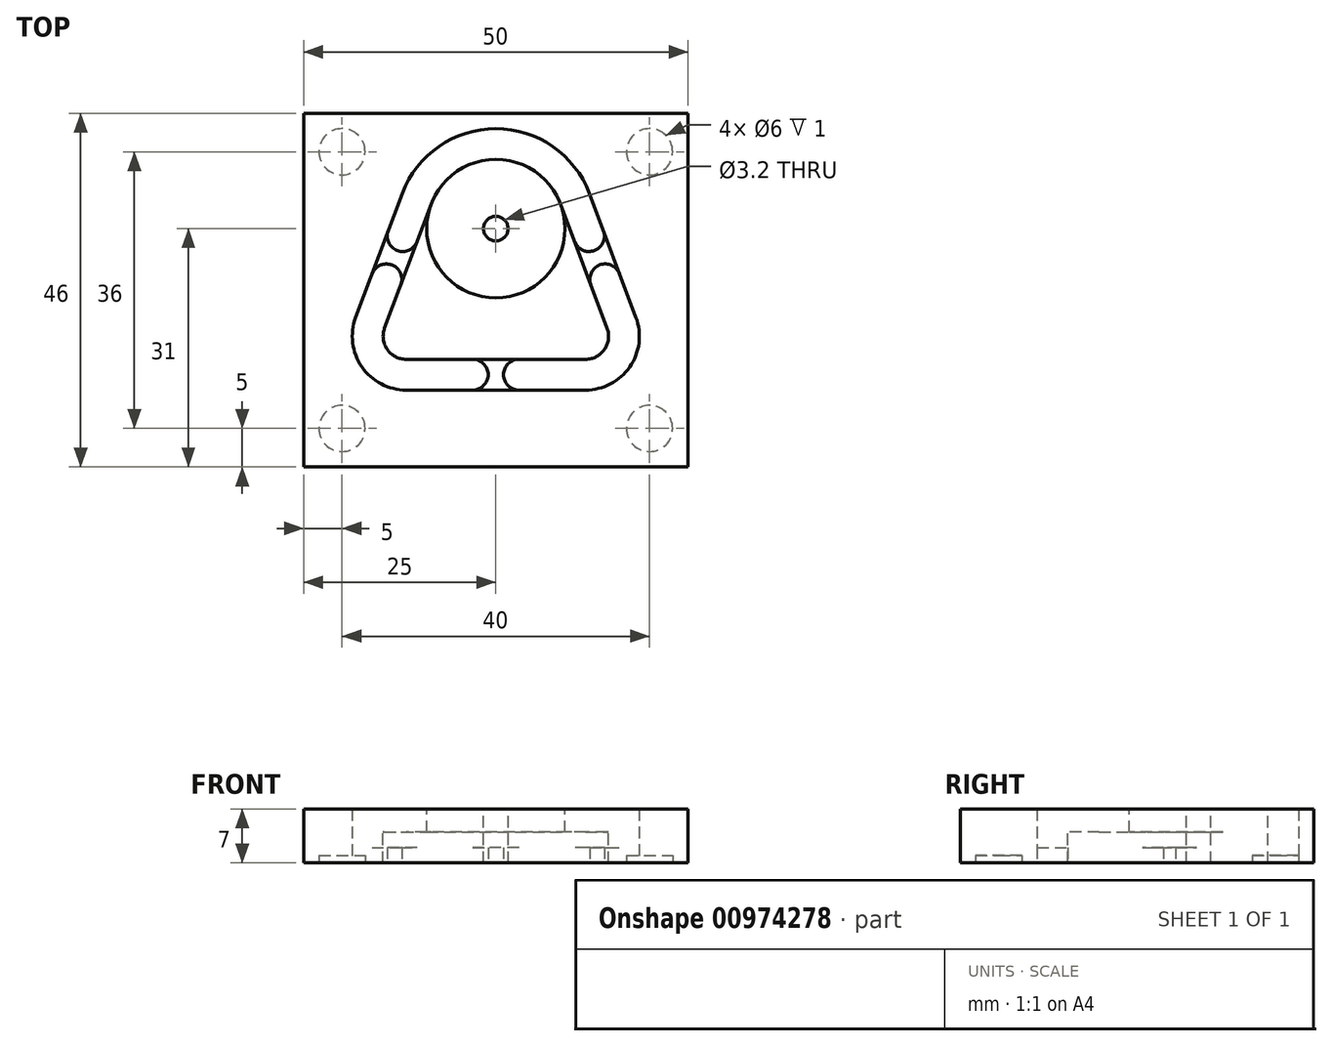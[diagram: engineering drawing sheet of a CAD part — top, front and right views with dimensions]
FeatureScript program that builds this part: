
annotation { "Feature Type Name" : "Feature", "Feature Type Description" : "" }
export const myFeature = defineFeature(function(context is Context, id is Id, definition is map)
    precondition{}
    {
        {
            var Q0;
            Q0=qCreatedBy(makeId("Top.planeOp"),FACE);
            var sketch = newSketch(context, id + "F0", { "sketchPlane" : qUnion([Q0])});
            skCircle(sketch, "E0", {"center": v(0, 0) * mm, "radius": 9 * mm});
            skLineSegment(sketch, "E1", {"start": v(0, 0) * mm, "end": v(0, -17) * mm, "construction": true});
            skLineSegment(sketch, "E2", {"start": v(0, -17) * mm, "end": v(-11.67, -17) * mm});
            skLineSegment(sketch, "E3", {"start": v(-14.48, -12.95) * mm, "end": v(-8.43, 3.16) * mm});
            skLineSegment(sketch, "E4", {"start": v(0, -17) * mm, "end": v(11.67, -17) * mm});
            skLineSegment(sketch, "E5", {"start": v(14.48, -12.95) * mm, "end": v(8.43, 3.16) * mm});
            skPoint(sketch, "E6.visualSharp", {"position": v(-16, -17) * mm});
            skArc(sketch, "E6.filletArc", {"start": v(-14.48, -12.95) * mm, "mid": v(-14.13, -15.7) * mm, "end": v(-11.67, -17) * mm});
            skPoint(sketch, "E7.visualSharp", {"position": v(16, -17) * mm});
            skArc(sketch, "E7.filletArc", {"start": v(11.67, -17) * mm, "mid": v(14.13, -15.7) * mm, "end": v(14.48, -12.95) * mm});
            skCircle(sketch, "E8", {"center": v(0, 0) * mm, "radius": 1.6 * mm});
            skSolve(sketch);
        }
        {
            var Q0;
            {var subQ0=sQuery(id+"F0.wireOp",EDGE,"E0");var subQ1=makeQuery(id+"F0.imprint","INTERSECT",VERTEX,{"derivedFrom":[subQ0,sQuery(id+"F0.wireOp",EDGE,"E3")]});Q0=makeQuery(id+"F0.imprint","IMPRINT",FACE,{"disambiguationData":[TD([[makeQuery(id+"F0.imprint","IMPRINT",EDGE,{"disambiguationData":[TD([[subQ1,1.0]])],"derivedFrom":subQ0}),1.0]])]});}
            var Q1;
            Q1=makeQuery(id+"F0.imprint","IMPRINT",FACE,{"disambiguationData":[TD([[makeQuery(id+"F0.imprint","IMPRINT",EDGE,{"derivedFrom":sQuery(id+"F0.wireOp",EDGE,"E2")}),-1.0]])]});
            extrude(context, id + "F1", {"entities" : qUnion([Q0, Q1]), "oppositeDirection" : true, "depth" : 3 * mm, "offsetDistance" : 25 * mm});
        }
        {
            var Q0;
            {var subQ0=sQuery(id+"F0.wireOp",EDGE,"E0");var subQ1=makeQuery(id+"F0.imprint","INTERSECT",VERTEX,{"derivedFrom":[subQ0,sQuery(id+"F0.wireOp",EDGE,"E3")]});Q0=makeQuery(id+"F0.imprint","IMPRINT",FACE,{"disambiguationData":[TD([[makeQuery(id+"F0.imprint","IMPRINT",EDGE,{"disambiguationData":[TD([[subQ1,1.0]])],"derivedFrom":subQ0}),1.0]])]});}
            extrude(context, id + "F2", {"entities" : qUnion([Q0]), "operationType" : NewBodyOperationType.ADD, "depth" : 3 * mm, "offsetDistance" : 25 * mm});
        }
        {
            var Q0;
            Q0=makeQuery(id+"F1.opExtrude","CAP_FACE",FACE,{"disambiguationData":[OSD([sQuery(id+"F0.wireOp",EDGE,"E0"),sQuery(id+"F0.wireOp",EDGE,"E2"),sQuery(id+"F0.wireOp",EDGE,"E3"),sQuery(id+"F0.wireOp",EDGE,"E4"),sQuery(id+"F0.wireOp",EDGE,"E5"),sQuery(id+"F0.wireOp",EDGE,"E6.filletArc"),sQuery(id+"F0.wireOp",EDGE,"E7.filletArc"),sQuery(id+"F0.wireOp",EDGE,"E8")])],"isStart":false});
            var sketch = newSketch(context, id + "F3", { "sketchPlane" : qUnion([Q0])});
            skLineSegment(sketch, "E9.0", {"start": v(-18.22, 11.54) * mm, "end": v(-12.17, -4.57) * mm});
            skLineSegment(sketch, "E9.1", {"start": v(12.17, -4.57) * mm, "end": v(18.22, 11.54) * mm});
            skArc(sketch, "E9.2", {"start": v(18.22, 11.54) * mm, "mid": v(17.42, 17.99) * mm, "end": v(11.67, 21) * mm});
            skArc(sketch, "E9.3", {"start": v(-12.17, -4.57) * mm, "mid": v(0, -13) * mm, "end": v(12.17, -4.57) * mm});
            skLineSegment(sketch, "E9.4", {"start": v(11.67, 21) * mm, "end": v(-11.67, 21) * mm});
            skArc(sketch, "E9.5", {"start": v(-11.67, 21) * mm, "mid": v(-17.42, 17.99) * mm, "end": v(-18.22, 11.54) * mm});
            skLineSegment(sketch, "E10.bottom", {"start": v(-25, -15) * mm, "end": v(25, -15) * mm});
            skLineSegment(sketch, "E10.top", {"start": v(-25, 31) * mm, "end": v(25, 31) * mm});
            skLineSegment(sketch, "E10.left", {"start": v(-25, -15) * mm, "end": v(-25, 31) * mm});
            skLineSegment(sketch, "E10.right", {"start": v(25, -15) * mm, "end": v(25, 31) * mm});
            skLineSegment(sketch, "E11", {"start": v(0, -15) * mm, "end": v(0, 31) * mm, "construction": true});
            skCircle(sketch, "E12", {"center": v(-20, -10) * mm, "radius": 5 * mm, "construction": true});
            skCircle(sketch, "E13", {"center": v(-20, -10) * mm, "radius": 3 * mm, "construction": true});
            skPoint(sketch, "E14", {"position": v(-20, -15) * mm});
            skCircle(sketch, "E15", {"center": v(-20, 26) * mm, "radius": 5 * mm, "construction": true});
            skPoint(sketch, "E16", {"position": v(-20, 31) * mm});
            skCircle(sketch, "E17", {"center": v(-20, 26) * mm, "radius": 3 * mm, "construction": true});
            skCircle(sketch, "E18", {"center": v(20, -10) * mm, "radius": 5 * mm, "construction": true});
            skCircle(sketch, "E19", {"center": v(20, -10) * mm, "radius": 3 * mm, "construction": true});
            skCircle(sketch, "E20", {"center": v(20, 26) * mm, "radius": 3 * mm, "construction": true});
            skCircle(sketch, "E21", {"center": v(20, 26) * mm, "radius": 5 * mm, "construction": true});
            skSolve(sketch);
        }
        {
            var Q0;
            Q0=makeQuery(id+"F3.imprint","IMPRINT",FACE,{"disambiguationData":[TD([[makeQuery(id+"F3.imprint","IMPRINT",EDGE,{"derivedFrom":sQuery(id+"F3.wireOp",EDGE,"E19")}),1.0]])]});
            var Q1;
            Q1=makeQuery(id+"F3.imprint","IMPRINT",FACE,{"disambiguationData":[TD([[makeQuery(id+"F3.imprint","IMPRINT",EDGE,{"derivedFrom":sQuery(id+"F3.wireOp",EDGE,"E9.0")}),-1.0]])]});
            var Q2;
            Q2=makeQuery(id+"F3.imprint","IMPRINT",FACE,{"disambiguationData":[TD([[makeQuery(id+"F3.imprint","IMPRINT",EDGE,{"derivedFrom":sQuery(id+"F3.wireOp",EDGE,"E13")}),1.0]])]});
            var Q3;
            Q3=makeQuery(id+"F3.imprint","IMPRINT",FACE,{"disambiguationData":[TD([[makeQuery(id+"F3.imprint","IMPRINT",EDGE,{"derivedFrom":sQuery(id+"F3.wireOp",EDGE,"E17")}),1.0]])]});
            var Q4;
            Q4=makeQuery(id+"F3.imprint","IMPRINT",FACE,{"disambiguationData":[TD([[makeQuery(id+"F3.imprint","IMPRINT",EDGE,{"derivedFrom":sQuery(id+"F3.wireOp",EDGE,"E20")}),1.0]])]});
            var Q5;
            Q5=makeQuery(id+"F2.opExtrude","CAP_FACE",FACE,{"disambiguationData":[OSD([sQuery(id+"F0.wireOp",EDGE,"E0"),sQuery(id+"F0.wireOp",EDGE,"E8")])],"isStart":false});
            extrude(context, id + "F4", {"entities" : qUnion([Q0, Q1, Q2, Q3, Q4]), "endBound" : BoundingType.UP_TO_SURFACE, "oppositeDirection" : true, "depth" : 25 * mm, "endBoundEntityFace" : qUnion([Q5]), "offsetDistance" : 25 * mm});
        }
        {
            var Q0;
            Q0=makeQuery(id+"F1.opExtrude","CAP_FACE",FACE,{"disambiguationData":[OSD([sQuery(id+"F0.wireOp",EDGE,"E0"),sQuery(id+"F0.wireOp",EDGE,"E2"),sQuery(id+"F0.wireOp",EDGE,"E3"),sQuery(id+"F0.wireOp",EDGE,"E4"),sQuery(id+"F0.wireOp",EDGE,"E5"),sQuery(id+"F0.wireOp",EDGE,"E6.filletArc"),sQuery(id+"F0.wireOp",EDGE,"E7.filletArc"),sQuery(id+"F0.wireOp",EDGE,"E8")])],"isStart":false});
            var sketch = newSketch(context, id + "F5", { "sketchPlane" : qUnion([Q0])});
            skLineSegment(sketch, "E22", {"start": v(-12.36, 7.3) * mm, "end": v(-16.1, 5.9) * mm});
            skLineSegment(sketch, "E23", {"start": v(-16.1, 5.9) * mm, "end": v(-14, 0.28) * mm});
            skLineSegment(sketch, "E24", {"start": v(-14, 0.28) * mm, "end": v(-10.25, 1.68) * mm});
            skLineSegment(sketch, "E25", {"start": v(-10.25, 1.68) * mm, "end": v(-12.36, 7.3) * mm});
            skArc(sketch, "E26", {"start": v(-16.1, 5.9) * mm, "mid": v(-13.53, 4.72) * mm, "end": v(-12.36, 7.3) * mm});
            skArc(sketch, "E27", {"start": v(-10.25, 1.68) * mm, "mid": v(-12.82, 2.85) * mm, "end": v(-14, 0.28) * mm});
            skLineSegment(sketch, "E28", {"start": v(12.36, 7.3) * mm, "end": v(10.25, 1.68) * mm});
            skLineSegment(sketch, "E29", {"start": v(10.25, 1.68) * mm, "end": v(14, 0.28) * mm});
            skLineSegment(sketch, "E30", {"start": v(14, 0.28) * mm, "end": v(16.1, 5.9) * mm});
            skLineSegment(sketch, "E31", {"start": v(16.1, 5.9) * mm, "end": v(12.36, 7.3) * mm});
            skArc(sketch, "E32", {"start": v(14, 0.28) * mm, "mid": v(12.82, 2.85) * mm, "end": v(10.25, 1.68) * mm});
            skArc(sketch, "E33", {"start": v(12.36, 7.3) * mm, "mid": v(13.53, 4.72) * mm, "end": v(16.1, 5.9) * mm});
            skLineSegment(sketch, "E34.bottom", {"start": v(-3, 17) * mm, "end": v(3, 17) * mm});
            skLineSegment(sketch, "E34.top", {"start": v(-3, 21) * mm, "end": v(3, 21) * mm});
            skLineSegment(sketch, "E34.left", {"start": v(-3, 17) * mm, "end": v(-3, 21) * mm});
            skLineSegment(sketch, "E34.right", {"start": v(3, 17) * mm, "end": v(3, 21) * mm});
            skLineSegment(sketch, "E35", {"start": v(0, 0) * mm, "end": v(0, 17) * mm, "construction": true});
            skPoint(sketch, "E36", {"position": v(0, 17) * mm});
            skArc(sketch, "E37", {"start": v(3, 21) * mm, "mid": v(1, 19) * mm, "end": v(3, 17) * mm});
            skArc(sketch, "E38", {"start": v(-3, 17) * mm, "mid": v(-1, 19) * mm, "end": v(-3, 21) * mm});
            skSolve(sketch);
        }
        {
            var Q0;
            Q0=makeQuery(id+"F5.imprint","IMPRINT",FACE,{"disambiguationData":[TD([[makeQuery(id+"F5.imprint","IMPRINT",EDGE,{"derivedFrom":sQuery(id+"F5.wireOp",EDGE,"E23")}),1.0]])]});
            var Q1;
            Q1=makeQuery(id+"F5.imprint","IMPRINT",FACE,{"disambiguationData":[TD([[makeQuery(id+"F5.imprint","IMPRINT",EDGE,{"derivedFrom":sQuery(id+"F5.wireOp",EDGE,"E34.bottom")}),-1.0]])]});
            var Q2;
            Q2=makeQuery(id+"F5.imprint","IMPRINT",FACE,{"disambiguationData":[TD([[makeQuery(id+"F5.imprint","IMPRINT",EDGE,{"derivedFrom":sQuery(id+"F5.wireOp",EDGE,"E28")}),1.0]])]});
            extrude(context, id + "F6", {"entities" : qUnion([Q0, Q1, Q2]), "operationType" : NewBodyOperationType.ADD, "oppositeDirection" : true, "depth" : 1 * mm, "offsetDistance" : 25 * mm});
        }
        {
            var Q0;
            Q0=makeQuery(id+"F6.boolean.opBoolean","MERGE",FACE,{"derivedFrom":[makeQuery(id+"F1.opExtrude","CAP_FACE",FACE,{"disambiguationData":[OSD([sQuery(id+"F0.wireOp",EDGE,"E0"),sQuery(id+"F0.wireOp",EDGE,"E2"),sQuery(id+"F0.wireOp",EDGE,"E3"),sQuery(id+"F0.wireOp",EDGE,"E4"),sQuery(id+"F0.wireOp",EDGE,"E5"),sQuery(id+"F0.wireOp",EDGE,"E6.filletArc"),sQuery(id+"F0.wireOp",EDGE,"E7.filletArc"),sQuery(id+"F0.wireOp",EDGE,"E8")])],"isStart":false}),makeQuery(id+"F4.opExtrude","CAP_FACE",FACE,{"disambiguationData":[OSD([sQuery(id+"F3.wireOp",EDGE,"E9.0"),sQuery(id+"F3.wireOp",EDGE,"E9.1"),sQuery(id+"F3.wireOp",EDGE,"E9.2"),sQuery(id+"F3.wireOp",EDGE,"E9.3"),sQuery(id+"F3.wireOp",EDGE,"E9.4"),sQuery(id+"F3.wireOp",EDGE,"E9.5"),sQuery(id+"F3.wireOp",EDGE,"E10.bottom"),sQuery(id+"F3.wireOp",EDGE,"E10.top"),sQuery(id+"F3.wireOp",EDGE,"E10.left"),sQuery(id+"F3.wireOp",EDGE,"E10.right")])],"isStart":true}),makeQuery(id+"F6.opExtrude","CAP_FACE",FACE,{"disambiguationData":[OSD([sQuery(id+"F5.wireOp",EDGE,"E23"),sQuery(id+"F5.wireOp",EDGE,"E25"),sQuery(id+"F5.wireOp",EDGE,"E26"),sQuery(id+"F5.wireOp",EDGE,"E27")])],"isStart":true}),makeQuery(id+"F6.opExtrude","CAP_FACE",FACE,{"disambiguationData":[OSD([sQuery(id+"F5.wireOp",EDGE,"E28"),sQuery(id+"F5.wireOp",EDGE,"E30"),sQuery(id+"F5.wireOp",EDGE,"E32"),sQuery(id+"F5.wireOp",EDGE,"E33")])],"isStart":true}),makeQuery(id+"F6.opExtrude","CAP_FACE",FACE,{"disambiguationData":[OSD([sQuery(id+"F5.wireOp",EDGE,"E34.bottom"),sQuery(id+"F5.wireOp",EDGE,"E34.top"),sQuery(id+"F5.wireOp",EDGE,"E37"),sQuery(id+"F5.wireOp",EDGE,"E38")])],"isStart":true})]});
            extrude(context, id + "F7", {"entities" : qUnion([Q0]), "operationType" : NewBodyOperationType.ADD, "depth" : 1 * mm, "offsetDistance" : 25 * mm});
        }
        {
            var Q0;
            Q0=makeQuery(id+"F7.opExtrude","CAP_FACE",FACE,{"disambiguationData":[OSD([sQuery(id+"F0.wireOp",EDGE,"E0"),sQuery(id+"F0.wireOp",EDGE,"E2"),sQuery(id+"F0.wireOp",EDGE,"E3"),sQuery(id+"F0.wireOp",EDGE,"E4"),sQuery(id+"F0.wireOp",EDGE,"E5"),sQuery(id+"F0.wireOp",EDGE,"E6.filletArc"),sQuery(id+"F0.wireOp",EDGE,"E7.filletArc"),sQuery(id+"F0.wireOp",EDGE,"E8"),sQuery(id+"F3.wireOp",EDGE,"E9.0"),sQuery(id+"F3.wireOp",EDGE,"E9.1"),sQuery(id+"F3.wireOp",EDGE,"E9.2"),sQuery(id+"F3.wireOp",EDGE,"E9.3"),sQuery(id+"F3.wireOp",EDGE,"E9.4"),sQuery(id+"F3.wireOp",EDGE,"E9.5"),sQuery(id+"F3.wireOp",EDGE,"E10.bottom"),sQuery(id+"F3.wireOp",EDGE,"E10.top"),sQuery(id+"F3.wireOp",EDGE,"E10.left"),sQuery(id+"F3.wireOp",EDGE,"E10.right"),sQuery(id+"F5.wireOp",EDGE,"E23"),sQuery(id+"F5.wireOp",EDGE,"E25"),sQuery(id+"F5.wireOp",EDGE,"E26"),sQuery(id+"F5.wireOp",EDGE,"E27"),sQuery(id+"F5.wireOp",EDGE,"E28"),sQuery(id+"F5.wireOp",EDGE,"E30"),sQuery(id+"F5.wireOp",EDGE,"E32"),sQuery(id+"F5.wireOp",EDGE,"E33"),sQuery(id+"F5.wireOp",EDGE,"E34.bottom"),sQuery(id+"F5.wireOp",EDGE,"E34.top"),sQuery(id+"F5.wireOp",EDGE,"E37"),sQuery(id+"F5.wireOp",EDGE,"E38")])],"isStart":false});
            var sketch = newSketch(context, id + "F8", { "sketchPlane" : qUnion([Q0])});
            skCircle(sketch, "E39.0", {"center": v(-20, 26) * mm, "radius": 3 * mm});
            skCircle(sketch, "E39.1", {"center": v(20, 26) * mm, "radius": 3 * mm});
            skCircle(sketch, "E39.2", {"center": v(20, -10) * mm, "radius": 3 * mm});
            skCircle(sketch, "E39.3", {"center": v(-20, -10) * mm, "radius": 3 * mm});
            skSolve(sketch);
        }
        {
            var Q0;
            Q0=makeQuery(id+"F8.imprint","IMPRINT",FACE,{"disambiguationData":[TD([[makeQuery(id+"F8.imprint","IMPRINT",EDGE,{"derivedFrom":sQuery(id+"F8.wireOp",EDGE,"E39.0")}),1.0]])]});
            var Q1;
            Q1=makeQuery(id+"F8.imprint","IMPRINT",FACE,{"disambiguationData":[TD([[makeQuery(id+"F8.imprint","IMPRINT",EDGE,{"derivedFrom":sQuery(id+"F8.wireOp",EDGE,"E39.1")}),1.0]])]});
            var Q2;
            Q2=makeQuery(id+"F8.imprint","IMPRINT",FACE,{"disambiguationData":[TD([[makeQuery(id+"F8.imprint","IMPRINT",EDGE,{"derivedFrom":sQuery(id+"F8.wireOp",EDGE,"E39.2")}),1.0]])]});
            var Q3;
            Q3=makeQuery(id+"F8.imprint","IMPRINT",FACE,{"disambiguationData":[TD([[makeQuery(id+"F8.imprint","IMPRINT",EDGE,{"derivedFrom":sQuery(id+"F8.wireOp",EDGE,"E39.3")}),1.0]])]});
            extrude(context, id + "F9", {"entities" : qUnion([Q0, Q1, Q2, Q3]), "operationType" : NewBodyOperationType.REMOVE, "oppositeDirection" : true, "depth" : 1 * mm, "offsetDistance" : 25 * mm});
        }
    });
